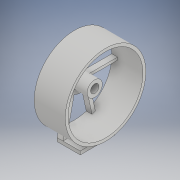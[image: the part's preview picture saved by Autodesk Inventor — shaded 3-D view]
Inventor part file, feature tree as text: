
AUTODESK INVENTOR PART (.ipt)
format: ipt  version: 2019 (Build 230136000, 136)  size: 253,440 bytes
history: native  units: in
note: dims shown in document units (in); Inventor stores cm internally (conversion verified against a paired STEP export)
features: sketch x13, extrude x12, projected_geometry x6
ambient origin geometry x8: Origin, YZ Plane, XZ Plane, XY Plane, X Axis, Y Axis, Z Axis, Center Point
bodies: Solid1 (feature_tree)
feature tree (31):
  extrude  "Extrusion1"  Depth=0.15in
  extrude  "Extrusion2"  Depth=0.1in TaperAngle=0.0deg
  extrude  "Extrusion3"  Depth=0.75in
  sketch  "Sketch6"  dims[d8=0.15in d9=0.25in d10=0.0in]
  extrude  "Extrusion7"  Depth=0.25in TaperAngle=0.0deg
  extrude  "Extrusion9"  Depth=0.875in TaperAngle=0.0deg
  extrude  "Extrusion10"  Depth=0.115in
  extrude  "Extrusion11"  Depth=0.05in
  extrude  "Extrusion12"  Depth=0.115in
  extrude  "Extrusion14"  Depth=0.05in
  extrude  "Extrusion15"  TaperAngle=0.0deg  [1 undecoded]
  extrude  "Extrusion16"  TaperAngle=0.0deg  [1 undecoded]
  extrude  "Extrusion17"  Depth=0.1in
  sketch  "Sketch1"  dims[d0=0.36in d1=0.15in]
  sketch  "Sketch2"  dims[d2=0.78in d3=0.0in d4=0.1in d5=0.0in]
  sketch  "Sketch3"  dims[d6=1.5in d7=0.75in]
  sketch  "Sketch10"  dims[d20=0.5315in d28=0.875in d29=0.0in]
  sketch  "Sketch13"  dims[d32=0.115in d33=0.115in]
  sketch  "Sketch14"  dims[d34=0.0675in d35=0.05in]
  projected_geometry  "Projected Loop9"
  projected_geometry  "Projected Loop10"
  projected_geometry  "Projected Loop11"
  projected_geometry  "Projected Loop12"
  sketch  "Sketch15"  dims[d36=0.115in d37=0.115in]
  sketch  "Sketch16"  dims[d38=0.068in d39=0.05in]
  sketch  "Sketch19"  dims[d40=0.15in d41=0.0in d42=0.0in]
  sketch  "Sketch20"  dims[d43=0.0in d44=0.0in]
  projected_geometry  "Projected Loop13"
  sketch  "Sketch21"  dims[d45=0.1in d46=0.0in d47=3.25in]
  projected_geometry  "Projected Loop14"
  sketch  "Sketch23"  dims[d48=3.5in d49=0.1in d50=0.0in d51=3.25in d52=1.25in d53=0.0in d82=0.25in d83=0.0in d84=0.25in d85=0.0in d86=0.25in d87=0.0in d88=0.75in d89=0.0in]
note: 2 required parameter values undecoded (feature->parameter linkage not recoverable at this tier; creation-order binding heuristic only, values carry confidence <= 0.55)
